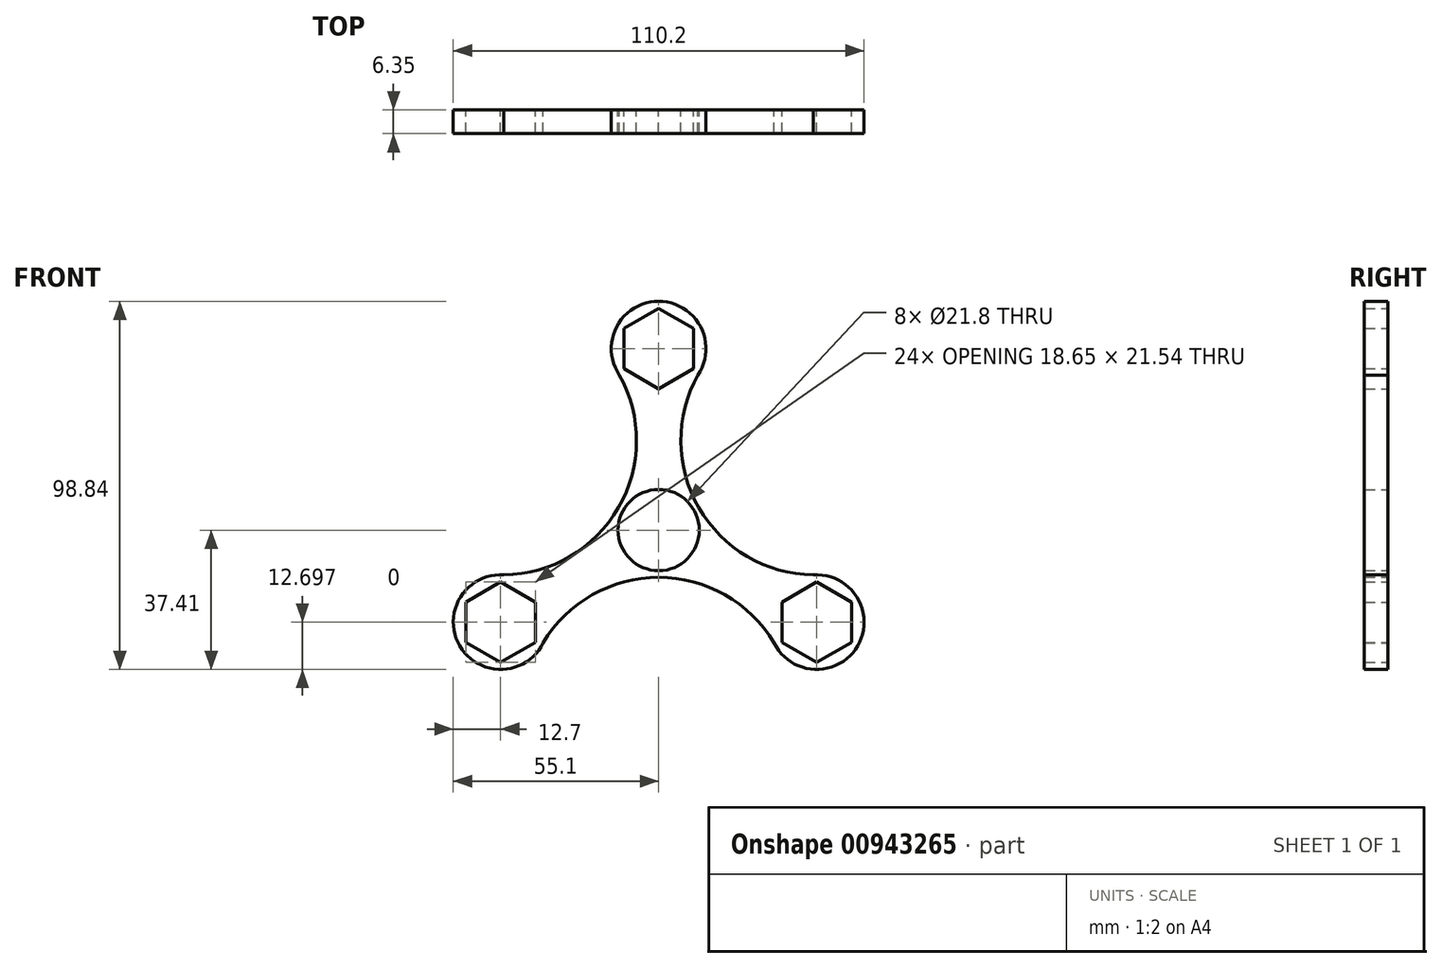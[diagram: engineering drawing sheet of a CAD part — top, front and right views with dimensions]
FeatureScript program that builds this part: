
annotation { "Feature Type Name" : "Feature", "Feature Type Description" : "" }
export const myFeature = defineFeature(function(context is Context, id is Id, definition is map)
    precondition{}
    {
        {
            var Q0;
            Q0=qCreatedBy(makeId("Front.planeOp"),FACE);
            var sketch = newSketch(context, id + "F0", { "sketchPlane" : qUnion([Q0])});
            skCircle(sketch, "E0", {"center": v(0, 0) * mm, "radius": 10.9 * mm});
            skCircle(sketch, "E1", {"center": v(0, 48.73) * mm, "radius": 12.7 * mm});
            skCircle(sketch, "E2.cCircle", {"center": v(0, 48.73) * mm, "radius": 9.32 * mm, "construction": true});
            skLineSegment(sketch, "E2.0", {"start": v(9.32, 54.11) * mm, "end": v(9.32, 43.34) * mm});
            skLineSegment(sketch, "E2.1", {"start": v(9.33, 43.34) * mm, "end": v(0, 37.96) * mm});
            skLineSegment(sketch, "E2.2", {"start": v(0, 37.96) * mm, "end": v(-9.33, 43.34) * mm});
            skLineSegment(sketch, "E2.3", {"start": v(-9.32, 43.34) * mm, "end": v(-9.33, 54.11) * mm});
            skLineSegment(sketch, "E2.4", {"start": v(-9.33, 54.11) * mm, "end": v(0, 59.5) * mm});
            skLineSegment(sketch, "E2.5", {"start": v(0, 59.5) * mm, "end": v(9.32, 54.11) * mm});
            skPoint(sketch, "E2.0.midPoint", {"position": v(9.32, 48.73) * mm});
            skArc(sketch, "E3", {"start": v(-11.43, 4.94) * mm, "mid": v(-5.96, 23.96) * mm, "end": v(-11.34, 43.01) * mm});
            skArc(sketch, "E4.MirrorCS", {"start": v(11.43, 4.94) * mm, "mid": v(5.96, 23.96) * mm, "end": v(11.34, 43.01) * mm});
            skArc(sketch, "E5.1.0", {"start": v(-11.43, 4.94) * mm, "mid": v(-25.01, -7.77) * mm, "end": v(-43.12, -12.03) * mm});
            skArc(sketch, "E5.1.1", {"start": v(1.24, -12.72) * mm, "mid": v(-17.97, -17.49) * mm, "end": v(-31.78, -31.68) * mm});
            skCircle(sketch, "E5.1.2", {"center": v(-42.4, -24.71) * mm, "radius": 12.7 * mm});
            skLineSegment(sketch, "E5.1.3", {"start": v(-42.4, -13.95) * mm, "end": v(-33.08, -19.33) * mm});
            skLineSegment(sketch, "E5.1.4", {"start": v(-33.08, -19.33) * mm, "end": v(-33.08, -30.1) * mm});
            skLineSegment(sketch, "E5.1.5", {"start": v(-51.73, -30.1) * mm, "end": v(-51.73, -19.33) * mm});
            skLineSegment(sketch, "E5.1.6", {"start": v(-51.73, -19.33) * mm, "end": v(-42.4, -13.95) * mm});
            skLineSegment(sketch, "E5.1.7", {"start": v(-42.4, -35.48) * mm, "end": v(-51.73, -30.1) * mm});
            skLineSegment(sketch, "E5.1.8", {"start": v(-33.08, -30.1) * mm, "end": v(-42.4, -35.48) * mm});
            skArc(sketch, "E5.2.0", {"start": v(1.24, -12.72) * mm, "mid": v(19.04, -18.12) * mm, "end": v(31.78, -31.68) * mm});
            skArc(sketch, "E5.2.1", {"start": v(11.43, 4.94) * mm, "mid": v(25.01, -7.77) * mm, "end": v(43.12, -12.03) * mm});
            skCircle(sketch, "E5.2.2", {"center": v(42.4, -24.71) * mm, "radius": 12.7 * mm});
            skLineSegment(sketch, "E5.2.3", {"start": v(33.08, -30.1) * mm, "end": v(33.08, -19.33) * mm});
            skLineSegment(sketch, "E5.2.4", {"start": v(33.08, -19.33) * mm, "end": v(42.4, -13.95) * mm});
            skLineSegment(sketch, "E5.2.5", {"start": v(51.73, -30.1) * mm, "end": v(42.4, -35.48) * mm});
            skLineSegment(sketch, "E5.2.6", {"start": v(42.4, -35.48) * mm, "end": v(33.08, -30.1) * mm});
            skLineSegment(sketch, "E5.2.7", {"start": v(51.73, -19.33) * mm, "end": v(51.73, -30.1) * mm});
            skLineSegment(sketch, "E5.2.8", {"start": v(42.4, -13.95) * mm, "end": v(51.73, -19.33) * mm});
            skPoint(sketch, "E5.center", {"position": v(0, -0.23) * mm});
            skPoint(sketch, "E6.orphan", {"position": v(-9.65, 8.14) * mm});
            skPoint(sketch, "E7.orphan", {"position": v(2.42, -12.78) * mm});
            skPoint(sketch, "E8.orphan", {"position": v(-2.42, -12.78) * mm});
            skPoint(sketch, "E9.orphan", {"position": v(9.65, 8.14) * mm});
            skPoint(sketch, "E10.trimOffspring.end.orphan", {"position": v(12.07, 3.94) * mm});
            skPoint(sketch, "E11.trimOffspring.start.orphan", {"position": v(-12.07, 3.94) * mm});
            skSolve(sketch);
        }
        {
            var Q0;
            Q0 = qSketchRegion(id + "F0", true);
            extrude(context, id + "F1", {"entities" : qUnion([Q0]), "depth" : 6.35 * mm, "offsetDistance" : 25.4 * mm});
        }
    });
